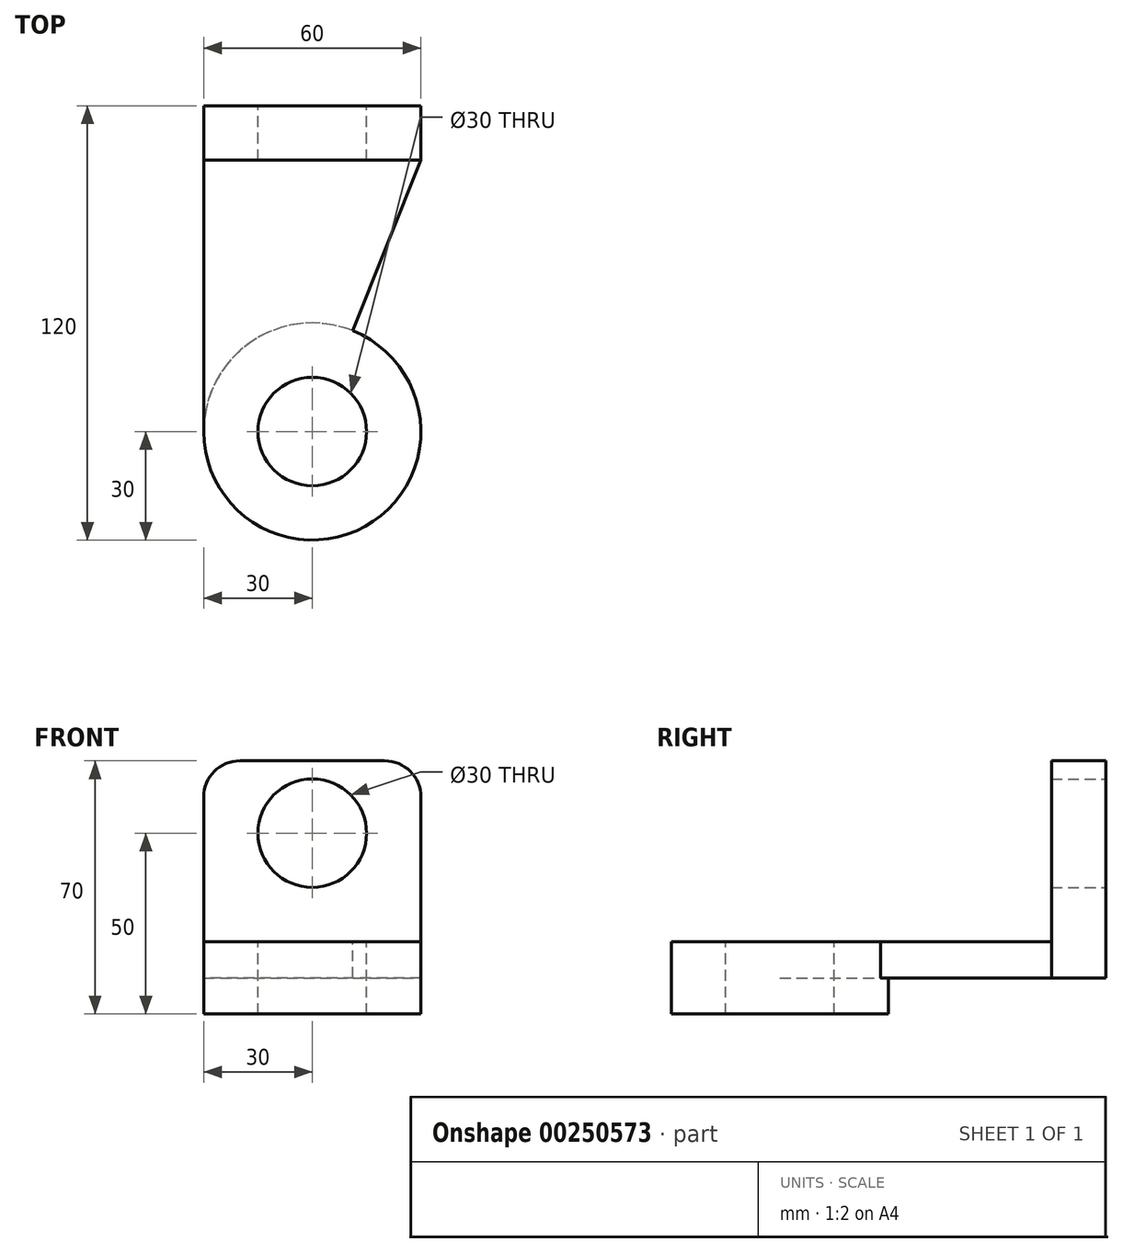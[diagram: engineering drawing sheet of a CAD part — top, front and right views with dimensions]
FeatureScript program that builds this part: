
annotation { "Feature Type Name" : "Feature", "Feature Type Description" : "" }
export const myFeature = defineFeature(function(context is Context, id is Id, definition is map)
    precondition{}
    {
        {
            var Q0;
            Q0=qCreatedBy(makeId("Front.planeOp"),FACE);
            var sketch = newSketch(context, id + "F0", { "sketchPlane" : qUnion([Q0])});
            skLineSegment(sketch, "E0.bottom", {"start": v(20, 25) * mm, "end": v(-20, 25) * mm});
            skLineSegment(sketch, "E0.top", {"start": v(30, -25) * mm, "end": v(-30, -25) * mm});
            skLineSegment(sketch, "E0.left", {"start": v(30, 15) * mm, "end": v(30, -25) * mm});
            skLineSegment(sketch, "E0.right", {"start": v(-30, 15) * mm, "end": v(-30, -25) * mm});
            skPoint(sketch, "E0.middle", {"position": v(0, 0) * mm});
            skPoint(sketch, "E1.visualSharp", {"position": v(-30, 25) * mm});
            skArc(sketch, "E1.filletArc", {"start": v(-20, 25) * mm, "mid": v(-27.07, 22.07) * mm, "end": v(-30, 15) * mm});
            skPoint(sketch, "E2.visualSharp", {"position": v(30, 25) * mm});
            skArc(sketch, "E2.filletArc", {"start": v(30, 15) * mm, "mid": v(27.07, 22.07) * mm, "end": v(20, 25) * mm});
            skCircle(sketch, "E3", {"center": v(0, 5) * mm, "radius": 15 * mm});
            skSolve(sketch);
        }
        {
            var Q0;
            Q0=makeQuery(id+"F0.imprint","IMPRINT",FACE,{"disambiguationData":[TD([[makeQuery(id+"F0.imprint","IMPRINT",EDGE,{"derivedFrom":sQuery(id+"F0.wireOp",EDGE,"E0.bottom")}),1.0]])]});
            extrude(context, id + "F1", {"entities" : qUnion([Q0]), "depth" : 15 * mm});
        }
        {
            var Q0;
            Q0=makeQuery(id+"F1.opExtrude","SWEPT_FACE",FACE,{"disambiguationData":[OSD([sQuery(id+"F0.wireOp",EDGE,"E0.top")])]});
            var sketch = newSketch(context, id + "F2", { "sketchPlane" : qUnion([Q0])});
            skCircle(sketch, "E4", {"center": v(0, 90) * mm, "radius": 30 * mm});
            skCircle(sketch, "E5", {"center": v(0, 90) * mm, "radius": 15 * mm});
            skLineSegment(sketch, "E6", {"start": v(-30, 15) * mm, "end": v(-30, 0) * mm});
            skLineSegment(sketch, "E7", {"start": v(-30, 0) * mm, "end": v(30, 0) * mm});
            skLineSegment(sketch, "E8", {"start": v(-30, 0) * mm, "end": v(-30, 90) * mm});
            skLineSegment(sketch, "E9.trimOffspring", {"start": v(11.14, 62.15) * mm, "end": v(30, 15) * mm});
            skLineSegment(sketch, "E10", {"start": v(30, 0) * mm, "end": v(30, 15) * mm});
            skSolve(sketch);
        }
        {
            var Q0;
            Q0 = qSketchRegion(id + "F2", true);
            extrude(context, id + "F3", {"entities" : qUnion([Q0]), "operationType" : NewBodyOperationType.ADD, "depth" : 10 * mm});
        }
        {
            var Q0;
            Q0=makeQuery(id+"F3.opExtrude","CAP_FACE",FACE,{"disambiguationData":[OSD([sQuery(id+"F2.wireOp",EDGE,"4mbg2ljK-9mCh-ITUw-ATVe-GDaMBGE4QUwJ"),sQuery(id+"F2.wireOp",EDGE,"E4"),sQuery(id+"F2.wireOp",EDGE,"E5"),sQuery(id+"F2.wireOp",EDGE,"tI7uqOMj-6m9N-elmy-9JB1-rdlYi8kl5VZa"),sQuery(id+"F2.wireOp",EDGE,"E6"),sQuery(id+"F2.wireOp",EDGE,"E7")])],"isStart":false});
            var sketch = newSketch(context, id + "F4", { "sketchPlane" : qUnion([Q0])});
            skCircle(sketch, "E11", {"center": v(0, 90) * mm, "radius": 15 * mm});
            skCircle(sketch, "E12", {"center": v(0, 90) * mm, "radius": 30 * mm});
            skSolve(sketch);
        }
        {
            var Q0;
            Q0 = qSketchRegion(id + "F4", true);
            extrude(context, id + "F5", {"entities" : qUnion([Q0]), "operationType" : NewBodyOperationType.ADD, "depth" : 10 * mm});
        }
    });
